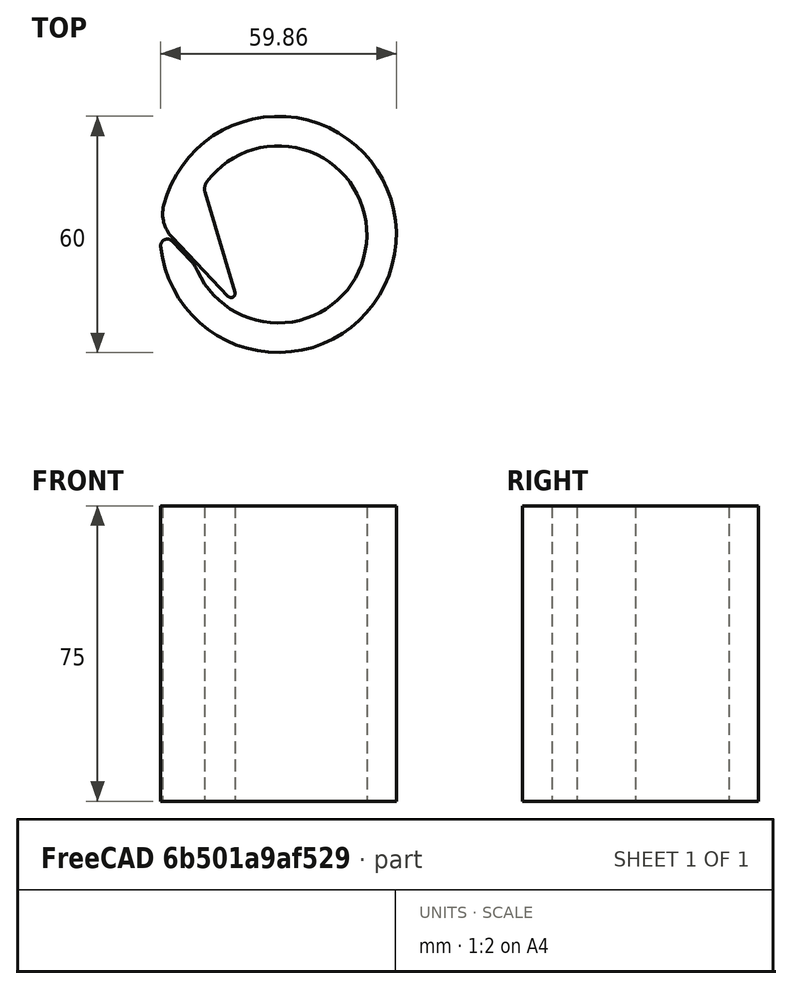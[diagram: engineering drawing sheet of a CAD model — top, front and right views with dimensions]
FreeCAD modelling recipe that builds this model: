
FCSTD DOCUMENT  (FreeCAD 0.22R38261 (Git))
Label: отцеп под свинец
License: All rights reserved
LicenseURL: https://en.wikipedia.org/wiki/All_rights_reserved
objects: Sketcher::SketchObject×3, PartDesign::Pad×1, PartDesign::Body×1, App::Part×1
note: 7 computed .brp shape members not serialized (recipe doc carries the construction recipe); baked Part::Feature solids carry a one-line shape summary decoded from their .brp

FEATURE [Sketcher::SketchObject] Sketch001  label="Kolco"
  AttachmentSupport = -> [XY_Plane]
  FullyConstrained = false
  MapMode = 5
  sketch-geometry (3):
    g0: GeomPoint X=0 Y=38.5843 Z=0
    g1: Circle CenterX=0 CenterY=66.0843 CenterZ=0 NormalX=0 NormalY=0 NormalZ=1 AngleXU=0 Radius=27.5
    g2: Circle CenterX=0 CenterY=66.0843 CenterZ=0 NormalX=0 NormalY=0 NormalZ=1 AngleXU=0 Radius=24.5
  constraints (6):
    c: PointOnObject(g0,g-2)
    c: PointOnObject(g1,g-2)
    c: Diameter(g1) = 55
    c: PointOnObject(g0,g1)
    c: Coincident(g2,g1)
    c: Diameter(g2) = 49
FEATURE [Sketcher::SketchObject] Sketch  label="Otcep"
  AttachmentSupport = -> [XY_Plane001,XY_Plane]
  FullyConstrained = false
  MapMode = 5
  sketch-geometry (11):
    g0: ArcOfCircle CenterX=0 CenterY=0 CenterZ=0 NormalX=0 NormalY=0 NormalZ=1 AngleXU=0 Radius=30 StartAngle=3.24229 EndAngle=9.17845
    g1: ArcOfCircle CenterX=0 CenterY=0 CenterZ=0 NormalX=0 NormalY=0 NormalZ=1 AngleXU=0 Radius=22.5 StartAngle=3.56645 EndAngle=8.7933
    g2: LineSegment StartX=-22.1738 StartY=-6.7846 StartZ=0 EndX=-26.9916 EndY=-1.7063 EndZ=0
    g3: LineSegment StartX=-26.9916 StartY=-0.706304 StartZ=0 EndX=-12.7398 EndY=-15.7288 EndZ=0
    g4: LineSegment StartX=-11.0087 StartY=-14.727 StartZ=0 EndX=-18.6044 EndY=10.7092 EndZ=0
    g5: ArcOfCircle CenterX=-11.9939 CenterY=-15.0212 CenterZ=0 NormalX=0 NormalY=0 NormalZ=1 AngleXU=0 Radius=1.02813 StartAngle=3.90067 EndAngle=6.57337
    g6: GeomPoint X=-9.77702 Y=-18.8518 Z=0
    g7: ArcOfCircle CenterX=-28.1961 CenterY=-2.84903 CenterZ=0 NormalX=0 NormalY=0 NormalZ=1 AngleXU=0 Radius=1.66033 StartAngle=0.759078 EndAngle=3.24229
    g8: ArcOfCircle CenterX=-20.7481 CenterY=5.21686 CenterZ=0 NormalX=0 NormalY=0 NormalZ=1 AngleXU=0 Radius=8.60608 StartAngle=2.89526 EndAngle=3.90067
    g9: ArcOfCircle CenterX=-15.791 CenterY=11.5493 CenterZ=0 NormalX=0 NormalY=0 NormalZ=1 AngleXU=0 Radius=2.93617 StartAngle=2.51011 EndAngle=3.43178
    g10: ArcOfCircle CenterX=-28.7167 CenterY=-12.9919 CenterZ=0 NormalX=0 NormalY=0 NormalZ=1 AngleXU=0 Radius=9.01889 StartAngle=0.42486 EndAngle=0.759078
  constraints (22):
    c: Coincident(g1,g-1)
    c: Coincident(g0,g1)
    c: Diameter(g0) = 60
    c: Diameter(g1) = 45  'rvnutr'
    c: PointOnObject(g6,g3)
    c: PointOnObject(g6,g4)
    c: Tangent(g3,g5) = -1.5708
    c: Tangent(g4,g5) = -1.5708
    c: Tangent(g2,g7) = -1.5708
    c: Tangent(g0,g7) = -1.5708
    c: Tangent(g3,g8) = -1.5708
    c: Tangent(g0,g8) = -1.5708
    c: Distance(g2,g3) = 1
    c: Parallel(g2,g3)
    c: Vertical(g2,g3)
    c: Tangent(g4,g9) = 1.5708
    c: Tangent(g1,g9) = -1.5708
    c: Tangent(g2,g10) = -1.5708
    c: Tangent(g1,g10) = 1.5708
    c: Distance(g3,g4) = 2
    c: Distance(g2) = 7
    c: Distance(g2,g3) = 13
FEATURE [PartDesign::Pad] Pad
  Direction = (0,0,1)
  Length = 75
  Length2 = 10
  Profile = -> Sketch
  ReferenceAxis = -> Sketch [N_Axis]
  Suppressed = false
  Type = 0
FEATURE [PartDesign::Body] Body
  AllowCompound = false
  Group = -> [Sketch,Sketch001,Pad]
  Origin = -> Origin001
  Tip = -> Pad
FEATURE [App::Part] Part
  Group = -> [Body]
  Origin = -> Origin
FEATURE [Sketcher::SketchObject] Sketch002  label="Kolco001"
  AttachmentSupport = -> [XY_Plane002]
  FullyConstrained = false
  MapMode = 5
  sketch-geometry (3):
    g0: GeomPoint X=0 Y=38.5843 Z=0
    g1: Circle CenterX=0 CenterY=66.0843 CenterZ=0 NormalX=0 NormalY=0 NormalZ=1 AngleXU=0 Radius=27.5
    g2: Circle CenterX=0 CenterY=66.0843 CenterZ=0 NormalX=0 NormalY=0 NormalZ=1 AngleXU=0 Radius=24.5
  constraints (6):
    c: PointOnObject(g0,g-2)
    c: PointOnObject(g1,g-2)
    c: Diameter(g1) = 55
    c: PointOnObject(g0,g1)
    c: Coincident(g2,g1)
    c: Diameter(g2) = 49
